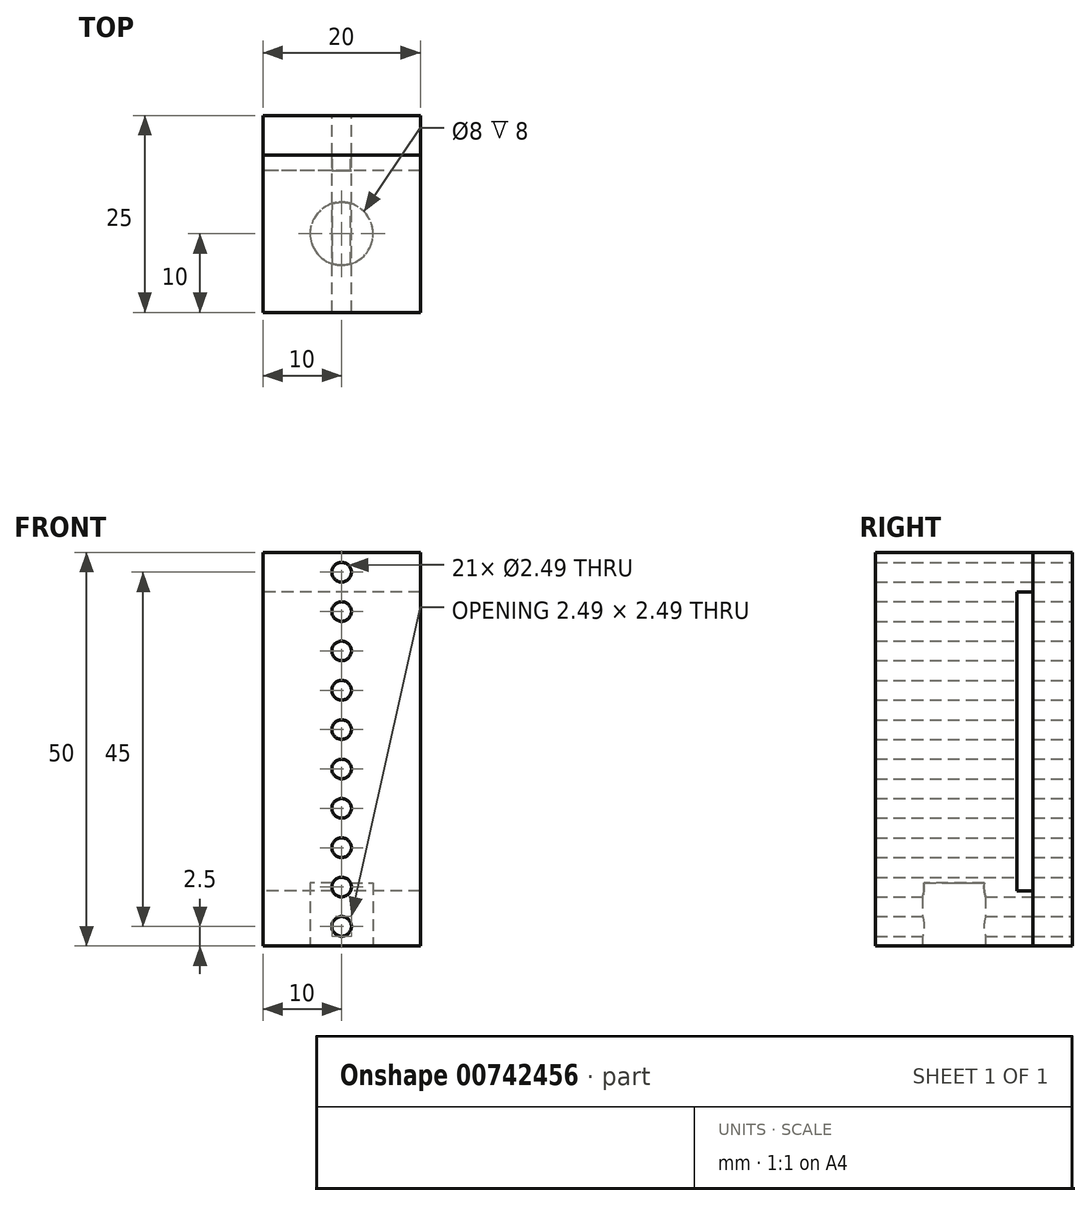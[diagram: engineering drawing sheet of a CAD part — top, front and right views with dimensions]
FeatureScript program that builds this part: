
annotation { "Feature Type Name" : "Feature", "Feature Type Description" : "" }
export const myFeature = defineFeature(function(context is Context, id is Id, definition is map)
    precondition{}
    {
        {
            var Q0;
            Q0=qCreatedBy(makeId("Top.planeOp"),FACE);
            var sketch = newSketch(context, id + "F0", { "sketchPlane" : qUnion([Q0])});
            skLineSegment(sketch, "E0.bottom", {"start": v(10, 10) * mm, "end": v(-10, 10) * mm});
            skLineSegment(sketch, "E0.top", {"start": v(10, -10) * mm, "end": v(-10, -10) * mm});
            skLineSegment(sketch, "E0.left", {"start": v(10, 10) * mm, "end": v(10, -10) * mm});
            skLineSegment(sketch, "E0.right", {"start": v(-10, 10) * mm, "end": v(-10, -10) * mm});
            skPoint(sketch, "E0.middle", {"position": v(0, 0) * mm});
            skSolve(sketch);
        }
        {
            var Q0;
            Q0 = qSketchRegion(id + "F0", true);
            extrude(context, id + "F1", {"entities" : qUnion([Q0]), "depth" : 50 * mm, "offsetDistance" : 25 * mm});
        }
        {
            var Q0;
            Q0=makeQuery(id+"F1.opExtrude","SWEPT_FACE",FACE,{"disambiguationData":[OSD([sQuery(id+"F0.wireOp",EDGE,"E0.bottom")])]});
            var sketch = newSketch(context, id + "F2", { "sketchPlane" : qUnion([Q0])});
            skLineSegment(sketch, "E1.bottom", {"start": v(-10, 45) * mm, "end": v(10, 45) * mm});
            skLineSegment(sketch, "E1.top", {"start": v(-10, 7) * mm, "end": v(10, 7) * mm});
            skLineSegment(sketch, "E1.left", {"start": v(-10, 45) * mm, "end": v(-10, 7) * mm});
            skLineSegment(sketch, "E1.right", {"start": v(10, 45) * mm, "end": v(10, 7) * mm});
            skSolve(sketch);
        }
        {
            var Q0;
            Q0=makeQuery(id+"F2.imprint","IMPRINT",FACE,{"disambiguationData":[TD([[makeQuery(id+"F2.imprint","IMPRINT",EDGE,{"derivedFrom":sQuery(id+"F2.wireOp",EDGE,"E1.bottom")}),-1.0]])]});
            extrude(context, id + "F3", {"entities" : qUnion([Q0]), "operationType" : NewBodyOperationType.REMOVE, "oppositeDirection" : true, "depth" : 2 * mm, "offsetDistance" : 25 * mm});
        }
        {
            var Q0;
            Q0=makeQuery(id+"F1.opExtrude","CAP_FACE",FACE,{"disambiguationData":[OSD([sQuery(id+"F0.wireOp",EDGE,"E0.bottom"),sQuery(id+"F0.wireOp",EDGE,"E0.top"),sQuery(id+"F0.wireOp",EDGE,"E0.left"),sQuery(id+"F0.wireOp",EDGE,"E0.right")])],"isStart":true});
            var sketch = newSketch(context, id + "F4", { "sketchPlane" : qUnion([Q0])});
            skCircle(sketch, "E2", {"center": v(0, 0) * mm, "radius": 4 * mm});
            skSolve(sketch);
        }
        {
            var Q0;
            Q0 = qSketchRegion(id + "F4", true);
            extrude(context, id + "F5", {"entities" : qUnion([Q0]), "operationType" : NewBodyOperationType.REMOVE, "oppositeDirection" : true, "depth" : 8 * mm, "offsetDistance" : 25 * mm});
        }
        {
            var Q0;
            {var subQ2=sQuery(id+"F0.wireOp",EDGE,"E0.bottom");Q0=makeQuery(id+"F3.boolean.opBoolean","SPLIT",FACE,{"disambiguationData":[TD([makeQuery(id+"F3.opExtrude","SWEPT_FACE",FACE,{"disambiguationData":[OSD([sQuery(id+"F2.wireOp",EDGE,"E1.bottom")])]})])],"derivedFrom":makeQuery(id+"F1.opExtrude","SWEPT_FACE",FACE,{"disambiguationData":[OSD([subQ2])]})});}
            var sketch = newSketch(context, id + "F6", { "sketchPlane" : qUnion([Q0])});
            skLineSegment(sketch, "E3.bottom", {"start": v(-10, 50) * mm, "end": v(10, 50) * mm});
            skLineSegment(sketch, "E3.top", {"start": v(-10, 0) * mm, "end": v(10, 0) * mm});
            skLineSegment(sketch, "E3.left", {"start": v(-10, 50) * mm, "end": v(-10, 0) * mm});
            skLineSegment(sketch, "E3.right", {"start": v(10, 50) * mm, "end": v(10, 0) * mm});
            skSolve(sketch);
        }
        {
            var Q0;
            Q0 = qSketchRegion(id + "F6", true);
            extrude(context, id + "F7", {"entities" : qUnion([Q0]), "depth" : 5 * mm, "offsetDistance" : 25 * mm});
        }
        {
            var Q0;
            Q0=makeQuery(id+"F7.opExtrude","CAP_FACE",FACE,{"disambiguationData":[OSD([sQuery(id+"F6.wireOp",EDGE,"E3.bottom"),sQuery(id+"F6.wireOp",EDGE,"E3.top"),sQuery(id+"F6.wireOp",EDGE,"E3.left"),sQuery(id+"F6.wireOp",EDGE,"E3.right")])],"isStart":false});
            var sketch = newSketch(context, id + "F8", { "sketchPlane" : qUnion([Q0])});
            skPoint(sketch, "E4", {"position": v(0, 50) * mm});
            skLineSegment(sketch, "E5", {"start": v(0, 50) * mm, "end": v(0, 0) * mm, "construction": true});
            skPoint(sketch, "E6", {"position": v(0, 45) * mm});
            skPoint(sketch, "E7", {"position": v(0, 47.5) * mm});
            skCircle(sketch, "E8", {"center": v(0, 47.5) * mm, "radius": 1.24 * mm});
            skCircle(sketch, "E9.0.1.0", {"center": v(0, 42.5) * mm, "radius": 1.24 * mm});
            skCircle(sketch, "E9.0.2.0", {"center": v(0, 37.5) * mm, "radius": 1.24 * mm});
            skCircle(sketch, "E9.0.3.0", {"center": v(0, 32.5) * mm, "radius": 1.24 * mm});
            skCircle(sketch, "E9.0.4.0", {"center": v(0, 27.5) * mm, "radius": 1.24 * mm});
            skCircle(sketch, "E9.0.5.0", {"center": v(0, 22.5) * mm, "radius": 1.24 * mm});
            skCircle(sketch, "E9.0.6.0", {"center": v(0, 17.5) * mm, "radius": 1.24 * mm});
            skCircle(sketch, "E9.0.7.0", {"center": v(0, 12.5) * mm, "radius": 1.24 * mm});
            skCircle(sketch, "E9.0.8.0", {"center": v(0, 7.5) * mm, "radius": 1.24 * mm});
            skCircle(sketch, "E9.0.9.0", {"center": v(0, 2.5) * mm, "radius": 1.24 * mm});
            skLineSegment(sketch, "E9.direction1", {"start": v(0, 47.5) * mm, "end": v(0, 47.5) * mm});
            skLineSegment(sketch, "E9.direction2", {"start": v(0, 47.5) * mm, "end": v(0, 42.5) * mm, "construction": true});
            skSolve(sketch);
        }
        {
            var Q0;
            Q0 = qSketchRegion(id + "F8", true);
            var Q1;
            Q1=makeQuery(id+"F3.boolean.opBoolean","COPY",FACE,{"derivedFrom":makeQuery(id+"F3.opExtrude","CAP_FACE",FACE,{"disambiguationData":[OSD([sQuery(id+"F2.wireOp",EDGE,"E1.bottom"),sQuery(id+"F2.wireOp",EDGE,"E1.top"),sQuery(id+"F2.wireOp",EDGE,"E1.left"),sQuery(id+"F2.wireOp",EDGE,"E1.right")])],"isStart":false})});
            extrude(context, id + "F9", {"entities" : qUnion([Q0]), "operationType" : NewBodyOperationType.REMOVE, "endBound" : BoundingType.THROUGH_ALL, "oppositeDirection" : true, "depth" : 19.1 * mm, "endBoundEntityFace" : qUnion([Q1]), "offsetDistance" : 25 * mm});
        }
    });
